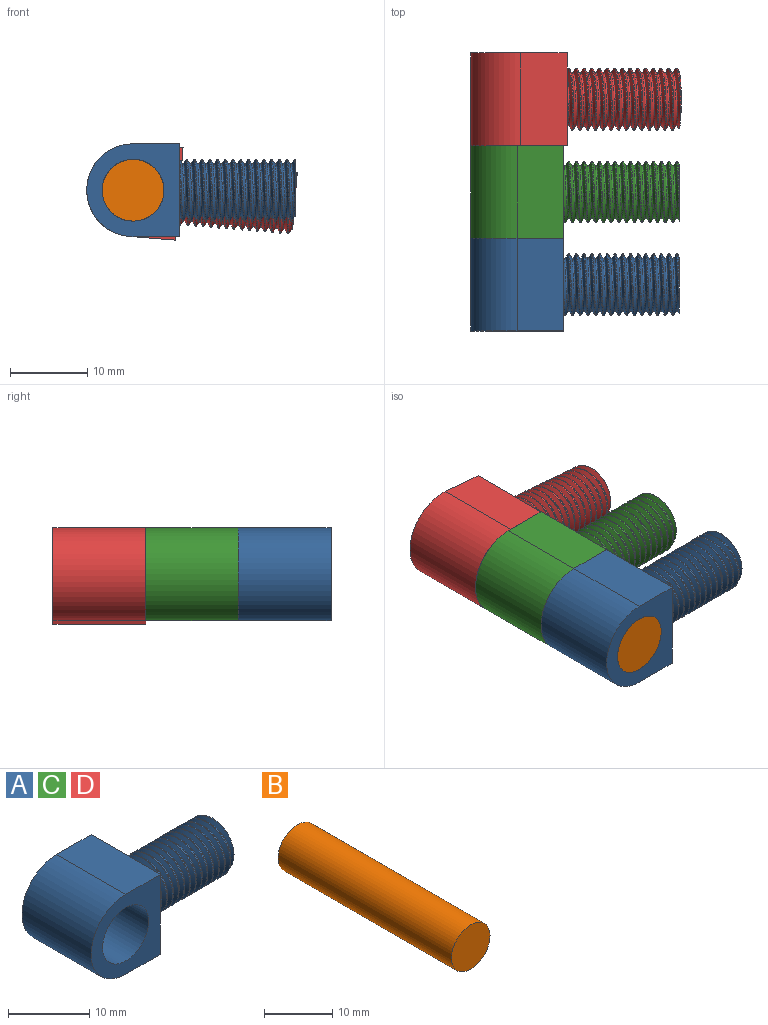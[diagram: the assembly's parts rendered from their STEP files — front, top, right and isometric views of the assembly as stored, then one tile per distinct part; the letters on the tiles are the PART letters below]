
ASSEMBLY  parts=4 mates=3
PART A: 12 faces, bbox 27.7x12.3x12.3 mm
  f0: plane 12x6mm, normal (0,0,-1), area 72mm2, adj f1,f4,f5,f11
  f1: plane 12.28x12.28mm, normal (1,0,0), area 101.2mm2, adj f0,f2,f4,f5,f6,f8,f9,f10
  f2: plane 12x6mm, normal (0,0,1), area 72mm2, adj f1,f4,f5,f11
  f3: cylinder r=4mm len=12mm, axis (0,1,0), area 301.6mm2, adj f4,f5
  f4: plane 12x12mm, normal (0,-1,0), area 78.3mm2, adj f0,f1,f2,f3,f11
  f5: plane 12x12mm, normal (0,1,0), area 78.3mm2, adj f0,f1,f2,f3,f11
  f6: cylinder r=4mm len=15mm, axis (-1,0,0), area 39.7mm2, adj f1,f7,f9,f10
  f7: plane 7.7x7.66mm, normal (1,0,0), area 42.8mm2, adj f6,f8,f9,f10
  f8: bspline ~15.75x7.99mm, area 90.5mm2, adj f1,f7,f9,f10
  f9: bspline ~15.81x9.24mm, area 220mm2, adj f1,f6,f7,f8
  f10: bspline ~15.65x9.24mm, area 219.5mm2, adj f1,f6,f7,f8
  f11: cylinder r=6mm len=12mm, axis (0,1,0), area 226.2mm2, adj f0,f2,f4,f5
PART B: 3 faces, bbox 8x36x8 mm
  f0: cylinder r=4mm len=36mm, axis (0,1,0), area 904.8mm2, adj f1,f2
  f1: plane 8x8mm, normal (0,-1,0), area 50.3mm2, adj f0
  f2: plane 8x8mm, normal (0,1,0), area 50.3mm2, adj f0
PART C: same geometry as A
PART D: same geometry as A
PLACE A t=(23.35,-43.28,9.87)mm
PLACE B rot(axis=(1,0,-0.04),180deg) t=(23.35,-43.28,9.87)mm
PLACE C t=(23.35,-31.28,9.87)mm
PLACE D rot(axis=(0,1,0),4.7deg) t=(23.35,-19.28,9.87)mm
MATE revolute B.f0 <-> A.f3  axis (0,-1,0) through (23.35,-49.28,9.87)mm
MATE revolute B.f0 <-> C.f3  axis (0,-1,0) through (23.35,-31.28,9.87)mm
MATE revolute B.f0 <-> D.f3  axis (0,-1,0) through (23.35,-13.28,9.87)mm
